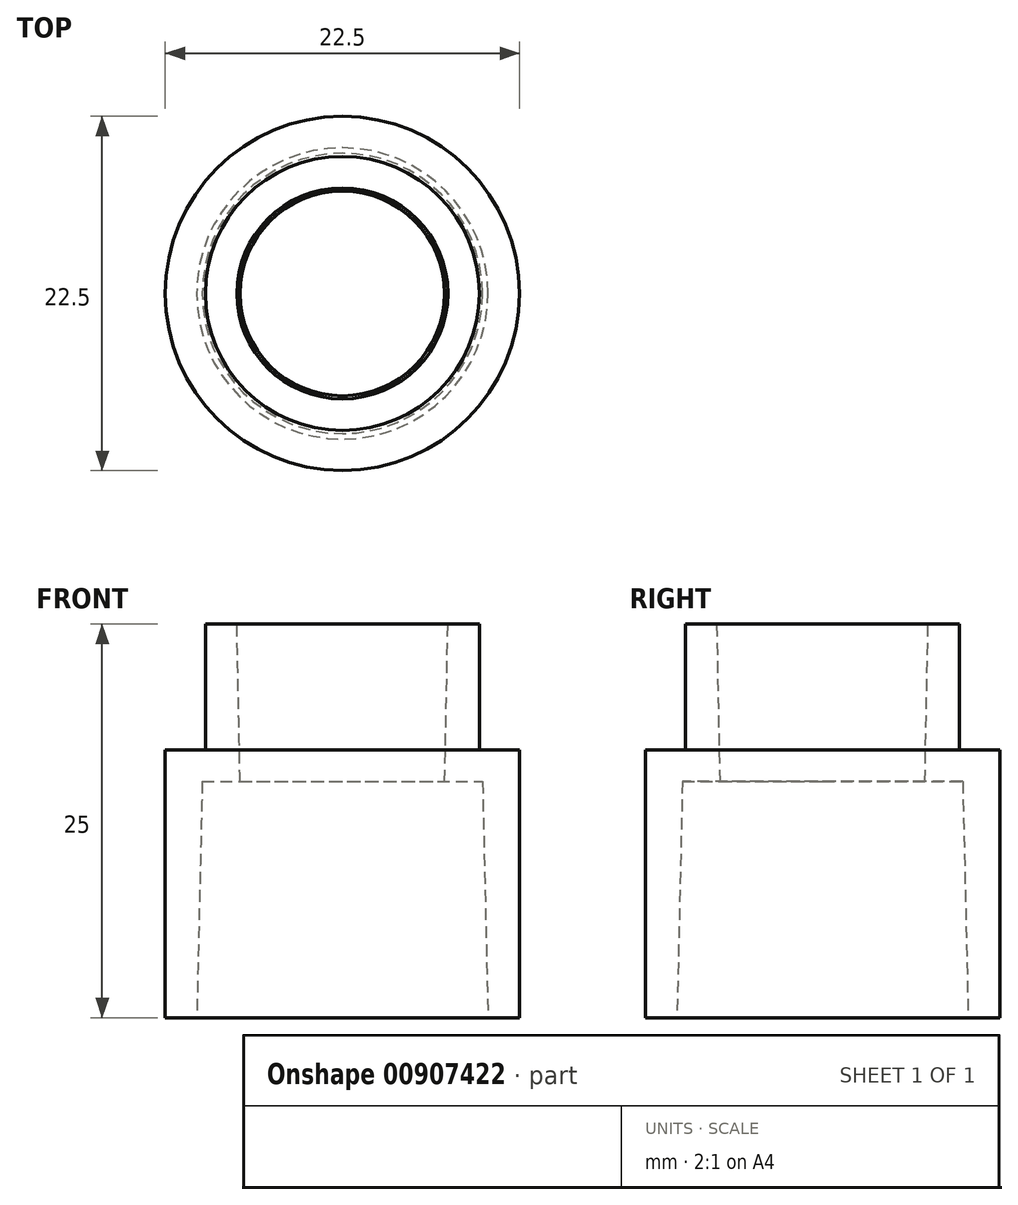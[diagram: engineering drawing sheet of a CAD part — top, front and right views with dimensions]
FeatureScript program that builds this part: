
annotation { "Feature Type Name" : "Feature", "Feature Type Description" : "" }
export const myFeature = defineFeature(function(context is Context, id is Id, definition is map)
    precondition{}
    {
        {
            var Q0;
            Q0=qCreatedBy(makeId("Front.planeOp"),FACE);
            var sketch = newSketch(context, id + "F0", { "sketchPlane" : qUnion([Q0])});
            skLineSegment(sketch, "E0", {"start": v(9.25, 0) * mm, "end": v(8.9, 15) * mm});
            skLineSegment(sketch, "E1", {"start": v(8.9, 15) * mm, "end": v(6.5, 15) * mm});
            skLineSegment(sketch, "E2", {"start": v(6.5, 15) * mm, "end": v(6.7, 25) * mm});
            skLineSegment(sketch, "E3", {"start": v(6.7, 25) * mm, "end": v(8.7, 25) * mm});
            skLineSegment(sketch, "E4", {"start": v(11.25, 17) * mm, "end": v(11.25, 0) * mm});
            skLineSegment(sketch, "E5", {"start": v(11.25, 0) * mm, "end": v(9.25, 0) * mm});
            skLineSegment(sketch, "E6", {"start": v(8.7, 25) * mm, "end": v(8.7, 17) * mm});
            skLineSegment(sketch, "E7", {"start": v(8.7, 17) * mm, "end": v(11.25, 17) * mm});
            skLineSegment(sketch, "E8", {"start": v(0, 0) * mm, "end": v(0, 51.02) * mm, "construction": true});
            skSolve(sketch);
        }
        {
            var Q0;
            Q0 = qSketchRegion(id + "F0", true);
            var Q1;
            Q1=sQuery(id+"F0.wireOp",EDGE,"E8");
            revolve(context, id + "F1", {"surfaceOperationType" : NewSurfaceOperationType.NEW, "entities" : qUnion([Q0]), "axis" : qUnion([Q1]), "revolveType" : RevolveType.FULL});
        }
    });
